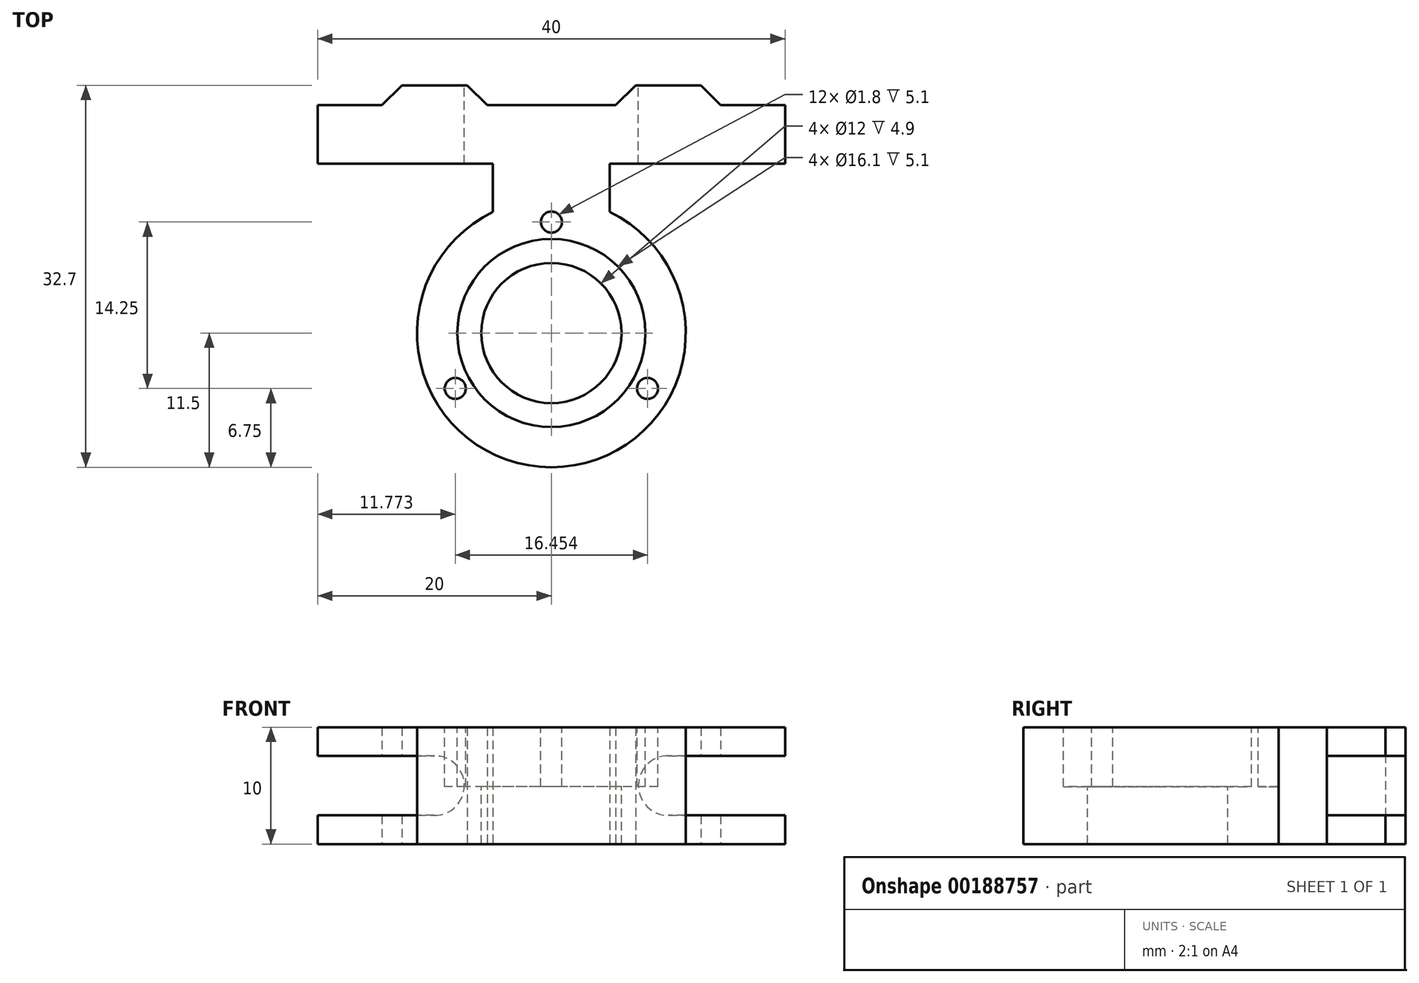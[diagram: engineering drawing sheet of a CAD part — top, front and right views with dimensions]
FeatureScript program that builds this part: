
annotation { "Feature Type Name" : "Feature", "Feature Type Description" : "" }
export const myFeature = defineFeature(function(context is Context, id is Id, definition is map)
    precondition{}
    {
        {
            var Q0;
            Q0=qCreatedBy(makeId("Top.planeOp"),FACE);
            var sketch = newSketch(context, id + "F0", { "sketchPlane" : qUnion([Q0])});
            skLineSegment(sketch, "E0.bottom", {"start": v(20, -11.5) * mm, "end": v(-20, -11.5) * mm});
            skLineSegment(sketch, "E0.left", {"start": v(20, -11.5) * mm, "end": v(20, 19.5) * mm});
            skLineSegment(sketch, "E0.right", {"start": v(-20, -11.5) * mm, "end": v(-20, 19.5) * mm});
            skPoint(sketch, "E0.middle", {"position": v(0, 0) * mm});
            skLineSegment(sketch, "E1", {"start": v(-20, 19.5) * mm, "end": v(-14.5, 19.5) * mm});
            skLineSegment(sketch, "E2", {"start": v(-14.5, 19.5) * mm, "end": v(-12.8, 21.2) * mm});
            skLineSegment(sketch, "E3", {"start": v(-12.8, 21.2) * mm, "end": v(-7.2, 21.2) * mm});
            skLineSegment(sketch, "E4", {"start": v(-7.2, 21.2) * mm, "end": v(-5.5, 19.5) * mm});
            skLineSegment(sketch, "E5", {"start": v(-5.5, 19.5) * mm, "end": v(5.5, 19.5) * mm});
            skLineSegment(sketch, "E6", {"start": v(5.5, 19.5) * mm, "end": v(7.2, 21.2) * mm});
            skLineSegment(sketch, "E7", {"start": v(7.2, 21.2) * mm, "end": v(12.8, 21.2) * mm});
            skLineSegment(sketch, "E8", {"start": v(12.8, 21.2) * mm, "end": v(14.5, 19.5) * mm});
            skLineSegment(sketch, "E9", {"start": v(14.5, 19.5) * mm, "end": v(20, 19.5) * mm});
            skLineSegment(sketch, "E10", {"start": v(0, -11.5) * mm, "end": v(0, 19.5) * mm, "construction": true});
            skLineSegment(sketch, "E11", {"start": v(-20, 14.5) * mm, "end": v(-5, 14.5) * mm});
            skLineSegment(sketch, "E12", {"start": v(-5, 14.5) * mm, "end": v(-5, 10.36) * mm});
            skLineSegment(sketch, "E13", {"start": v(-5, 10.36) * mm, "end": v(-20, 5.79) * mm});
            skLineSegment(sketch, "E14", {"start": v(20, 14.5) * mm, "end": v(5, 14.5) * mm});
            skLineSegment(sketch, "E15", {"start": v(5, 14.5) * mm, "end": v(5, 10.36) * mm});
            skLineSegment(sketch, "E16", {"start": v(5, 10.36) * mm, "end": v(20, 5.79) * mm});
            skCircle(sketch, "E17", {"center": v(0, 0) * mm, "radius": 11.5 * mm});
            skSolve(sketch);
        }
        {
            var Q0;
            {var subQ3=sQuery(id+"F0.wireOp",EDGE,"E1");Q0=makeQuery(id+"F0.imprint","IMPRINT",FACE,{"disambiguationData":[TD([[makeQuery(id+"F0.imprint","IMPRINT",EDGE,{"derivedFrom":subQ3}),-1.0]])]});}
            var Q1;
            {var subQ0=sQuery(id+"F0.wireOp",EDGE,"E17");var subQ3=makeQuery(id+"F0.imprint","INTERSECT",VERTEX,{"derivedFrom":[sQuery(id+"F0.wireOp",EDGE,"E0.bottom"),subQ0]});Q1=makeQuery(id+"F0.imprint","IMPRINT",FACE,{"disambiguationData":[TD([[makeQuery(id+"F0.imprint","IMPRINT",EDGE,{"disambiguationData":[TD([[subQ3,1.0]])],"derivedFrom":subQ0}),1.0]])]});}
            extrude(context, id + "F1", {"entities" : qUnion([Q0, Q1]), "depth" : 10 * mm, "offsetDistance" : 25 * mm});
        }
        {
            var Q0;
            Q0=makeQuery(id+"F1.opExtrude","CAP_FACE",FACE,{"disambiguationData":[OSD([sQuery(id+"F0.wireOp",EDGE,"E0.bottom"),sQuery(id+"F0.wireOp",EDGE,"E0.left"),sQuery(id+"F0.wireOp",EDGE,"E0.right"),sQuery(id+"F0.wireOp",EDGE,"E1"),sQuery(id+"F0.wireOp",EDGE,"E2"),sQuery(id+"F0.wireOp",EDGE,"E3"),sQuery(id+"F0.wireOp",EDGE,"E4"),sQuery(id+"F0.wireOp",EDGE,"E5"),sQuery(id+"F0.wireOp",EDGE,"E6"),sQuery(id+"F0.wireOp",EDGE,"E7"),sQuery(id+"F0.wireOp",EDGE,"E8"),sQuery(id+"F0.wireOp",EDGE,"E9")])],"isStart":false});
            var sketch = newSketch(context, id + "F2", { "sketchPlane" : qUnion([Q0])});
            skCircle(sketch, "E18", {"center": v(0, 0) * mm, "radius": 6 * mm});
            skCircle(sketch, "E19", {"center": v(0, 0) * mm, "radius": 8.05 * mm});
            skLineSegment(sketch, "E20", {"start": v(0, 0) * mm, "end": v(0, 7.92) * mm, "construction": true});
            skLineSegment(sketch, "E21", {"start": v(0, 0) * mm, "end": v(11.28, -6.51) * mm, "construction": true});
            skLineSegment(sketch, "E22", {"start": v(0, 0) * mm, "end": v(-12.53, -7.23) * mm, "construction": true});
            skCircle(sketch, "E23", {"center": v(0, 0) * mm, "radius": 9.5 * mm, "construction": true});
            skCircle(sketch, "E24", {"center": v(-8.23, -4.75) * mm, "radius": 0.9 * mm});
            skCircle(sketch, "E25", {"center": v(8.23, -4.75) * mm, "radius": 0.9 * mm});
            skCircle(sketch, "E26", {"center": v(0, 9.5) * mm, "radius": 0.9 * mm});
            skSolve(sketch);
        }
        {
            var Q0;
            Q0=makeQuery(id+"F2.imprint","IMPRINT",FACE,{"disambiguationData":[TD([[makeQuery(id+"F2.imprint","IMPRINT",EDGE,{"derivedFrom":sQuery(id+"F2.wireOp",EDGE,"E18")}),1.0]])]});
            extrude(context, id + "F3", {"entities" : qUnion([Q0]), "operationType" : NewBodyOperationType.REMOVE, "endBound" : BoundingType.UP_TO_NEXT, "oppositeDirection" : true, "depth" : 25 * mm, "offsetDistance" : 25 * mm});
        }
        {
            var Q0;
            Q0=makeQuery(id+"F2.imprint","IMPRINT",FACE,{"disambiguationData":[TD([[makeQuery(id+"F2.imprint","IMPRINT",EDGE,{"derivedFrom":sQuery(id+"F2.wireOp",EDGE,"E18")}),-1.0]])]});
            var Q1;
            Q1=makeQuery(id+"F2.imprint","IMPRINT",FACE,{"disambiguationData":[TD([[makeQuery(id+"F2.imprint","IMPRINT",EDGE,{"derivedFrom":sQuery(id+"F2.wireOp",EDGE,"E24")}),1.0]])]});
            var Q2;
            Q2=makeQuery(id+"F2.imprint","IMPRINT",FACE,{"disambiguationData":[TD([[makeQuery(id+"F2.imprint","IMPRINT",EDGE,{"derivedFrom":sQuery(id+"F2.wireOp",EDGE,"E26")}),1.0]])]});
            var Q3;
            Q3=makeQuery(id+"F2.imprint","IMPRINT",FACE,{"disambiguationData":[TD([[makeQuery(id+"F2.imprint","IMPRINT",EDGE,{"derivedFrom":sQuery(id+"F2.wireOp",EDGE,"E25")}),1.0]])]});
            extrude(context, id + "F4", {"entities" : qUnion([Q0, Q1, Q2, Q3]), "operationType" : NewBodyOperationType.REMOVE, "oppositeDirection" : true, "depth" : 5.1 * mm, "offsetDistance" : 25 * mm});
        }
        {
            var Q0;
            Q0=makeQuery(id+"F1.opExtrude","SWEPT_FACE",FACE,{"disambiguationData":[OSD([sQuery(id+"F0.wireOp",EDGE,"E7")])]});
            cPlane(context, id + "F5", {"entities" : qUnion([Q0]), "cplaneType" : CPlaneType.OFFSET, "offset" : 0 * mm, "width" : 150 * mm, "height" : 150 * mm});
        }
        {
            var Q0;
            Q0=qCreatedBy(id+"F5.planeOp",FACE);
            var sketch = newSketch(context, id + "F6", { "sketchPlane" : qUnion([Q0])});
            skCircle(sketch, "E27", {"center": v(-10, 5) * mm, "radius": 2.55 * mm});
            skCircle(sketch, "E28", {"center": v(10, 5) * mm, "radius": 2.55 * mm});
            skLineSegment(sketch, "E29", {"start": v(-10, 2.45) * mm, "end": v(-20, 2.45) * mm});
            skLineSegment(sketch, "E30", {"start": v(-10, 7.55) * mm, "end": v(-20, 7.55) * mm});
            skLineSegment(sketch, "E31", {"start": v(10, 7.55) * mm, "end": v(20, 7.55) * mm});
            skLineSegment(sketch, "E32", {"start": v(10, 2.45) * mm, "end": v(20, 2.45) * mm});
            skLineSegment(sketch, "E33", {"start": v(-20, 7.55) * mm, "end": v(-20, 2.45) * mm});
            skLineSegment(sketch, "E34", {"start": v(20, 7.55) * mm, "end": v(20, 2.45) * mm});
            skSolve(sketch);
        }
        {
            var Q0;
            {var subQ0=sQuery(id+"F6.wireOp",EDGE,"E28");var subQ1=makeQuery(id+"F6.imprint","INTERSECT",VERTEX,{"derivedFrom":[subQ0,sQuery(id+"F6.wireOp",EDGE,"E31")]});Q0=makeQuery(id+"F6.imprint","IMPRINT",FACE,{"disambiguationData":[TD([[makeQuery(id+"F6.imprint","IMPRINT",EDGE,{"disambiguationData":[TD([[subQ1,-1.0]])],"derivedFrom":subQ0}),1.0]])]});}
            var Q1;
            {var subQ0=sQuery(id+"F6.wireOp",EDGE,"E31");Q1=makeQuery(id+"F6.imprint","IMPRINT",FACE,{"disambiguationData":[TD([[makeQuery(id+"F6.imprint","IMPRINT",EDGE,{"derivedFrom":subQ0}),-1.0]])]});}
            var Q2;
            {var subQ0=sQuery(id+"F6.wireOp",EDGE,"E29");Q2=makeQuery(id+"F6.imprint","IMPRINT",FACE,{"disambiguationData":[TD([[makeQuery(id+"F6.imprint","IMPRINT",EDGE,{"derivedFrom":subQ0}),-1.0]])]});}
            var Q3;
            {var subQ0=sQuery(id+"F6.wireOp",EDGE,"E27");var subQ1=makeQuery(id+"F6.imprint","INTERSECT",VERTEX,{"derivedFrom":[subQ0,sQuery(id+"F6.wireOp",EDGE,"E29")]});Q3=makeQuery(id+"F6.imprint","IMPRINT",FACE,{"disambiguationData":[TD([[makeQuery(id+"F6.imprint","IMPRINT",EDGE,{"disambiguationData":[TD([[subQ1,1.0]])],"derivedFrom":subQ0}),1.0]])]});}
            var Q4;
            Q4=makeQuery(id+"F1.opExtrude","SWEPT_FACE",FACE,{"disambiguationData":[OSD([sQuery(id+"F0.wireOp",EDGE,"E11")])]});
            extrude(context, id + "F7", {"entities" : qUnion([Q0, Q1, Q2, Q3]), "operationType" : NewBodyOperationType.REMOVE, "endBound" : BoundingType.UP_TO_SURFACE, "oppositeDirection" : true, "depth" : 25 * mm, "endBoundEntityFace" : qUnion([Q4]), "offsetDistance" : 25 * mm});
        }
    });
